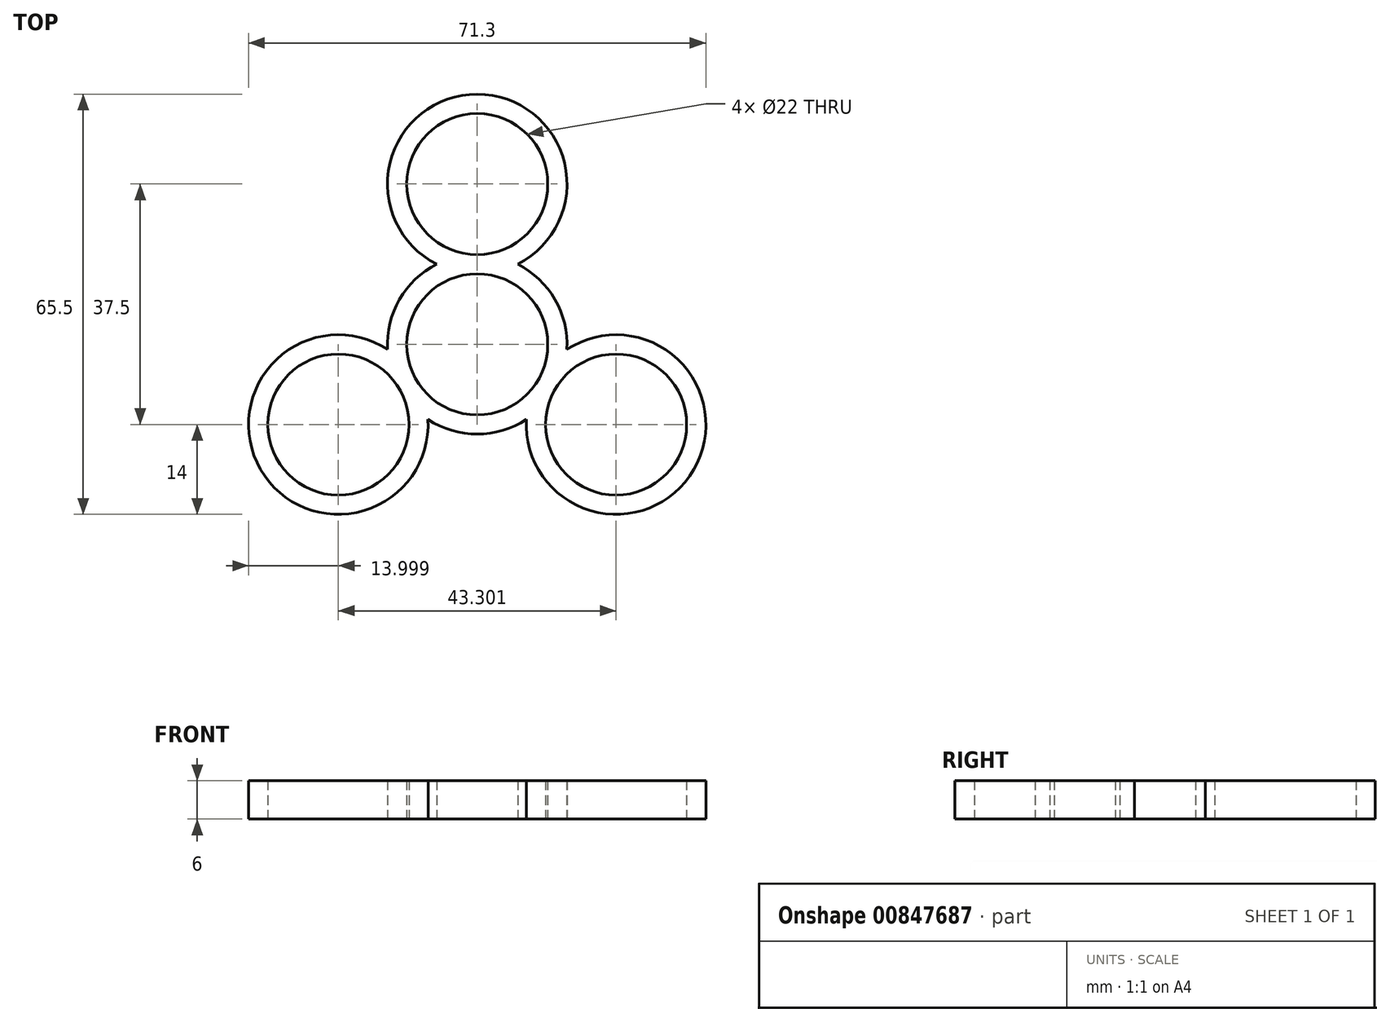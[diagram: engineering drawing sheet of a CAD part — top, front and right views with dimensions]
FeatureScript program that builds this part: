
annotation { "Feature Type Name" : "Feature", "Feature Type Description" : "" }
export const myFeature = defineFeature(function(context is Context, id is Id, definition is map)
    precondition{}
    {
        {
            var Q0;
            Q0=qCreatedBy(makeId("Top.planeOp"),FACE);
            var sketch = newSketch(context, id + "F0", { "sketchPlane" : qUnion([Q0])});
            skArc(sketch, "E0", {"start": v(9.53, 5.5) * mm, "mid": v(0, 11) * mm, "end": v(-9.53, 5.5) * mm});
            skCircle(sketch, "E1", {"center": v(0, 25) * mm, "radius": 11 * mm});
            skArc(sketch, "E2", {"start": v(6.3, 12.5) * mm, "mid": v(0, 39) * mm, "end": v(-6.3, 12.5) * mm});
            skArc(sketch, "E3", {"start": v(-6.3, 12.5) * mm, "mid": v(-9.62, 10.17) * mm, "end": v(-12.12, 7) * mm});
            skArc(sketch, "E4.trimOffspring", {"start": v(12.12, 7) * mm, "mid": v(9.62, 10.17) * mm, "end": v(6.3, 12.5) * mm});
            skArc(sketch, "E5.1.0", {"start": v(-13.98, -0.79) * mm, "mid": v(-33.77, -19.5) * mm, "end": v(-7.67, -11.71) * mm});
            skCircle(sketch, "E5.1.1", {"center": v(-21.65, -12.5) * mm, "radius": 11 * mm});
            skArc(sketch, "E5.1.2", {"start": v(-12.12, 7) * mm, "mid": v(-13.62, 3.24) * mm, "end": v(-13.98, -0.79) * mm});
            skArc(sketch, "E5.1.3", {"start": v(-9.53, 5.5) * mm, "mid": v(-9.53, -5.5) * mm, "end": v(0, -11) * mm});
            skArc(sketch, "E5.1.4", {"start": v(-7.67, -11.71) * mm, "mid": v(-4, -13.42) * mm, "end": v(0, -14) * mm});
            skArc(sketch, "E5.2.0", {"start": v(7.67, -11.71) * mm, "mid": v(33.77, -19.5) * mm, "end": v(13.98, -0.79) * mm});
            skCircle(sketch, "E5.2.1", {"center": v(21.65, -12.5) * mm, "radius": 11 * mm});
            skArc(sketch, "E5.2.2", {"start": v(0, -14) * mm, "mid": v(4, -13.42) * mm, "end": v(7.67, -11.71) * mm});
            skArc(sketch, "E5.2.3", {"start": v(0, -11) * mm, "mid": v(9.53, -5.5) * mm, "end": v(9.53, 5.5) * mm});
            skArc(sketch, "E5.2.4", {"start": v(13.98, -0.79) * mm, "mid": v(13.62, 3.24) * mm, "end": v(12.12, 7) * mm});
            skSolve(sketch);
        }
        {
            var Q0;
            Q0=makeQuery(id+"F0.imprint","IMPRINT",FACE,{"disambiguationData":[TD([[makeQuery(id+"F0.imprint","IMPRINT",EDGE,{"derivedFrom":sQuery(id+"F0.wireOp",EDGE,"E0")}),-1.0]])]});
            extrude(context, id + "F1", {"entities" : qUnion([Q0]), "depth" : 6 * mm, "offsetDistance" : 25 * mm});
        }
    });
